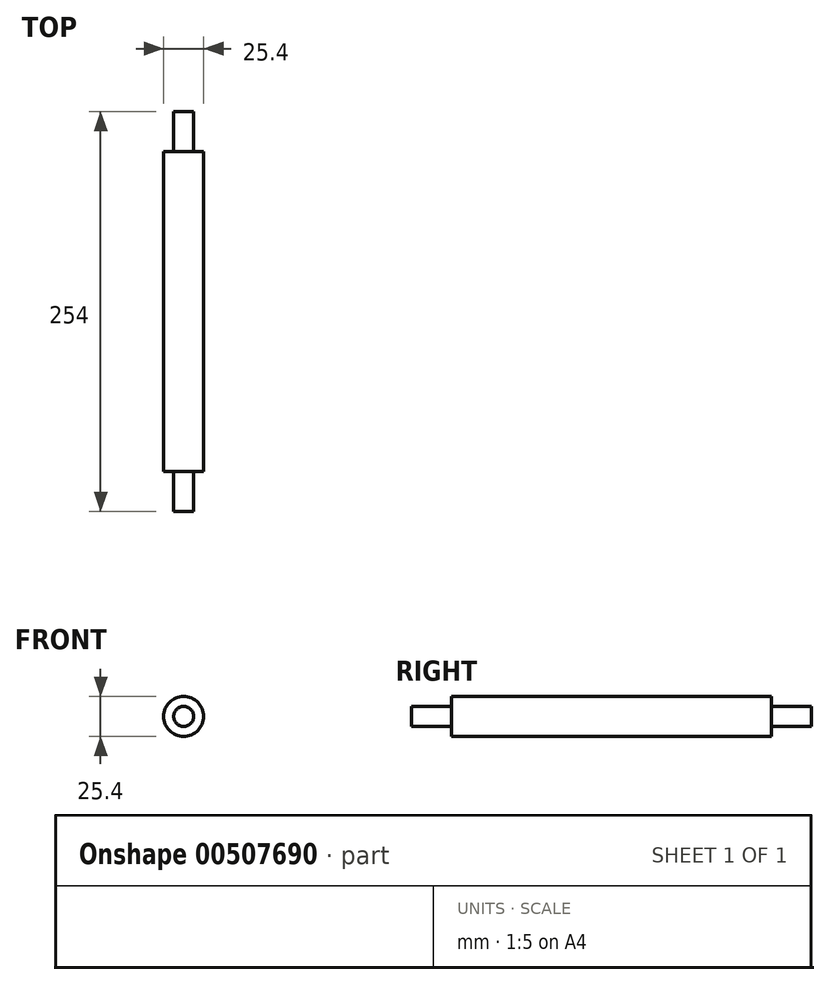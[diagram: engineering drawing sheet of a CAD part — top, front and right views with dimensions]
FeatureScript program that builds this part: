
annotation { "Feature Type Name" : "Feature", "Feature Type Description" : "" }
export const myFeature = defineFeature(function(context is Context, id is Id, definition is map)
    precondition{}
    {
        {
            var Q0;
            Q0=qCreatedBy(makeId("Front.planeOp"),FACE);
            var sketch = newSketch(context, id + "F0", { "sketchPlane" : qUnion([Q0])});
            skCircle(sketch, "E0", {"center": v(0, 0) * mm, "radius": 6.35 * mm});
            skSolve(sketch);
        }
        {
            var Q0;
            Q0 = qSketchRegion(id + "F0", true);
            extrude(context, id + "F1", {"entities" : qUnion([Q0]), "depth" : 25.4 * mm});
        }
        {
            var Q0;
            Q0=makeQuery(id+"F1.opExtrude","CAP_FACE",FACE,{"disambiguationData":[OSD([sQuery(id+"F0.wireOp",EDGE,"E0")])],"isStart":false});
            var sketch = newSketch(context, id + "F2", { "sketchPlane" : qUnion([Q0])});
            skCircle(sketch, "E1.0.0", {"center": v(0, 0) * mm, "radius": 6.35 * mm});
            skCircle(sketch, "E2", {"center": v(0, 0) * mm, "radius": 12.7 * mm});
            skSolve(sketch);
        }
        {
            var Q0;
            Q0=makeQuery(id+"F2.imprint","IMPRINT",FACE,{"disambiguationData":[TD([[makeQuery(id+"F2.imprint","IMPRINT",EDGE,{"derivedFrom":sQuery(id+"F2.wireOp",EDGE,"E1.0.0")}),1.0]])]});
            var Q1;
            Q1=makeQuery(id+"F2.imprint","IMPRINT",FACE,{"disambiguationData":[TD([[makeQuery(id+"F2.imprint","IMPRINT",EDGE,{"derivedFrom":sQuery(id+"F2.wireOp",EDGE,"E1.0.0")}),-1.0]])]});
            extrude(context, id + "F3", {"entities" : qUnion([Q0, Q1]), "operationType" : NewBodyOperationType.ADD, "depth" : 203.2 * mm});
        }
        {
            var Q0;
            Q0=makeQuery(id+"F3.opExtrude","CAP_FACE",FACE,{"disambiguationData":[OSD([sQuery(id+"F2.wireOp",EDGE,"E2")])],"isStart":false});
            var sketch = newSketch(context, id + "F4", { "sketchPlane" : qUnion([Q0])});
            skCircle(sketch, "E3.0.0", {"center": v(0, 0) * mm, "radius": 12.7 * mm});
            skCircle(sketch, "E4", {"center": v(0, 0) * mm, "radius": 6.35 * mm});
            skSolve(sketch);
        }
        {
            var Q0;
            Q0=makeQuery(id+"F4.imprint","IMPRINT",FACE,{"disambiguationData":[TD([[makeQuery(id+"F4.imprint","IMPRINT",EDGE,{"derivedFrom":sQuery(id+"F4.wireOp",EDGE,"E4")}),1.0]])]});
            extrude(context, id + "F5", {"entities" : qUnion([Q0]), "operationType" : NewBodyOperationType.ADD, "depth" : 25.4 * mm});
        }
    });
